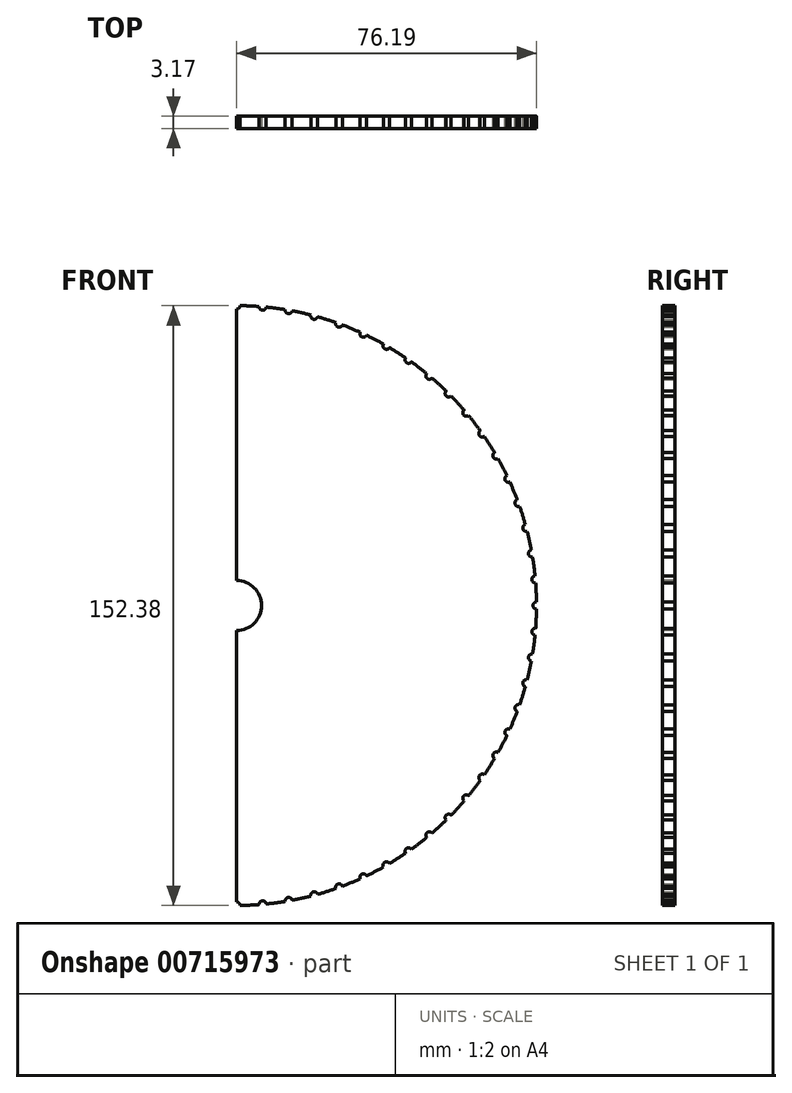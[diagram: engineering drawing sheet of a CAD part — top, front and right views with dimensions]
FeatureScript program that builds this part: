
annotation { "Feature Type Name" : "Feature", "Feature Type Description" : "" }
export const myFeature = defineFeature(function(context is Context, id is Id, definition is map)
    precondition{}
    {
        {
            var Q0;
            Q0=qCreatedBy(makeId("Front.planeOp"),FACE);
            var sketch = newSketch(context, id + "F0", { "sketchPlane" : qUnion([Q0])});
            skArc(sketch, "E0", {"start": v(-42.98, 62.93) * mm, "mid": v(-43.7, 62.42) * mm, "end": v(-44.43, 61.9) * mm});
            skCircle(sketch, "E1", {"center": v(0, 76.2) * mm, "radius": 0.89 * mm});
            skArc(sketch, "E2.1.0", {"start": v(-7.53, 75.83) * mm, "mid": v(-6.56, 75.02) * mm, "end": v(-5.76, 75.98) * mm});
            skCircle(sketch, "E2.2.0", {"center": v(-13.23, 75.04) * mm, "radius": 0.89 * mm});
            skCircle(sketch, "E2.3.0", {"center": v(-19.72, 73.6) * mm, "radius": 0.89 * mm});
            skCircle(sketch, "E2.4.0", {"center": v(-26.06, 71.6) * mm, "radius": 0.89 * mm});
            skCircle(sketch, "E2.5.0", {"center": v(-32.2, 69.06) * mm, "radius": 0.89 * mm});
            skCircle(sketch, "E2.6.0", {"center": v(-38.1, 66) * mm, "radius": 0.89 * mm});
            skCircle(sketch, "E2.7.0", {"center": v(-43.7, 62.42) * mm, "radius": 0.89 * mm});
            skCircle(sketch, "E2.8.0", {"center": v(-48.98, 58.37) * mm, "radius": 0.89 * mm});
            skCircle(sketch, "E2.9.0", {"center": v(-53.88, 53.88) * mm, "radius": 0.89 * mm});
            skCircle(sketch, "E2.10.0", {"center": v(-58.37, 48.98) * mm, "radius": 0.89 * mm});
            skCircle(sketch, "E2.11.0", {"center": v(-62.42, 43.7) * mm, "radius": 0.89 * mm});
            skCircle(sketch, "E2.12.0", {"center": v(-66, 38.1) * mm, "radius": 0.89 * mm});
            skCircle(sketch, "E2.13.0", {"center": v(-69.06, 32.2) * mm, "radius": 0.89 * mm});
            skCircle(sketch, "E2.14.0", {"center": v(-71.6, 26.06) * mm, "radius": 0.89 * mm});
            skCircle(sketch, "E2.15.0", {"center": v(-73.6, 19.72) * mm, "radius": 0.89 * mm});
            skCircle(sketch, "E2.16.0", {"center": v(-75.04, 13.23) * mm, "radius": 0.89 * mm});
            skCircle(sketch, "E2.17.0", {"center": v(-75.91, 6.64) * mm, "radius": 0.89 * mm});
            skCircle(sketch, "E2.18.0", {"center": v(-76.2, 0) * mm, "radius": 0.89 * mm});
            skCircle(sketch, "E2.19.0", {"center": v(-75.91, -6.64) * mm, "radius": 0.89 * mm});
            skCircle(sketch, "E2.20.0", {"center": v(-75.04, -13.23) * mm, "radius": 0.89 * mm});
            skCircle(sketch, "E2.21.0", {"center": v(-73.6, -19.72) * mm, "radius": 0.89 * mm});
            skCircle(sketch, "E2.22.0", {"center": v(-71.6, -26.06) * mm, "radius": 0.89 * mm});
            skCircle(sketch, "E2.23.0", {"center": v(-69.06, -32.2) * mm, "radius": 0.89 * mm});
            skCircle(sketch, "E2.24.0", {"center": v(-66, -38.1) * mm, "radius": 0.89 * mm});
            skCircle(sketch, "E2.25.0", {"center": v(-62.42, -43.7) * mm, "radius": 0.89 * mm});
            skCircle(sketch, "E2.26.0", {"center": v(-58.37, -48.98) * mm, "radius": 0.89 * mm});
            skCircle(sketch, "E2.27.0", {"center": v(-53.88, -53.88) * mm, "radius": 0.89 * mm});
            skCircle(sketch, "E2.28.0", {"center": v(-48.98, -58.37) * mm, "radius": 0.89 * mm});
            skCircle(sketch, "E2.29.0", {"center": v(-43.7, -62.42) * mm, "radius": 0.89 * mm});
            skCircle(sketch, "E2.30.0", {"center": v(-38.1, -66) * mm, "radius": 0.89 * mm});
            skCircle(sketch, "E2.31.0", {"center": v(-32.2, -69.06) * mm, "radius": 0.89 * mm});
            skCircle(sketch, "E2.32.0", {"center": v(-26.06, -71.6) * mm, "radius": 0.89 * mm});
            skCircle(sketch, "E2.33.0", {"center": v(-19.72, -73.6) * mm, "radius": 0.89 * mm});
            skCircle(sketch, "E2.34.0", {"center": v(-13.23, -75.04) * mm, "radius": 0.89 * mm});
            skCircle(sketch, "E2.35.0", {"center": v(-6.64, -75.91) * mm, "radius": 0.89 * mm});
            skCircle(sketch, "E2.36.0", {"center": v(0, -76.2) * mm, "radius": 0.89 * mm});
            skCircle(sketch, "E2.37.0", {"center": v(6.64, -75.91) * mm, "radius": 0.89 * mm});
            skCircle(sketch, "E2.38.0", {"center": v(13.23, -75.04) * mm, "radius": 0.89 * mm});
            skCircle(sketch, "E2.39.0", {"center": v(19.72, -73.6) * mm, "radius": 0.89 * mm});
            skCircle(sketch, "E2.40.0", {"center": v(26.06, -71.6) * mm, "radius": 0.89 * mm});
            skCircle(sketch, "E2.41.0", {"center": v(32.2, -69.06) * mm, "radius": 0.89 * mm});
            skCircle(sketch, "E2.42.0", {"center": v(38.1, -66) * mm, "radius": 0.89 * mm});
            skCircle(sketch, "E2.43.0", {"center": v(43.7, -62.42) * mm, "radius": 0.89 * mm});
            skCircle(sketch, "E2.44.0", {"center": v(48.98, -58.37) * mm, "radius": 0.89 * mm});
            skCircle(sketch, "E2.45.0", {"center": v(53.88, -53.88) * mm, "radius": 0.89 * mm});
            skCircle(sketch, "E2.46.0", {"center": v(58.37, -48.98) * mm, "radius": 0.89 * mm});
            skCircle(sketch, "E2.47.0", {"center": v(62.42, -43.7) * mm, "radius": 0.89 * mm});
            skCircle(sketch, "E2.48.0", {"center": v(66, -38.1) * mm, "radius": 0.89 * mm});
            skCircle(sketch, "E2.49.0", {"center": v(69.06, -32.2) * mm, "radius": 0.89 * mm});
            skCircle(sketch, "E2.50.0", {"center": v(71.6, -26.06) * mm, "radius": 0.89 * mm});
            skCircle(sketch, "E2.51.0", {"center": v(73.6, -19.72) * mm, "radius": 0.89 * mm});
            skCircle(sketch, "E2.52.0", {"center": v(75.04, -13.23) * mm, "radius": 0.89 * mm});
            skCircle(sketch, "E2.53.0", {"center": v(75.91, -6.64) * mm, "radius": 0.89 * mm});
            skCircle(sketch, "E2.54.0", {"center": v(76.2, 0) * mm, "radius": 0.89 * mm});
            skCircle(sketch, "E2.55.0", {"center": v(75.91, 6.64) * mm, "radius": 0.89 * mm});
            skCircle(sketch, "E2.56.0", {"center": v(75.04, 13.23) * mm, "radius": 0.89 * mm});
            skCircle(sketch, "E2.57.0", {"center": v(73.6, 19.72) * mm, "radius": 0.89 * mm});
            skCircle(sketch, "E2.58.0", {"center": v(71.6, 26.06) * mm, "radius": 0.89 * mm});
            skCircle(sketch, "E2.59.0", {"center": v(69.06, 32.2) * mm, "radius": 0.89 * mm});
            skCircle(sketch, "E2.60.0", {"center": v(66, 38.1) * mm, "radius": 0.89 * mm});
            skCircle(sketch, "E2.61.0", {"center": v(62.42, 43.7) * mm, "radius": 0.89 * mm});
            skCircle(sketch, "E2.62.0", {"center": v(58.37, 48.98) * mm, "radius": 0.89 * mm});
            skCircle(sketch, "E2.63.0", {"center": v(53.88, 53.88) * mm, "radius": 0.89 * mm});
            skCircle(sketch, "E2.64.0", {"center": v(48.98, 58.37) * mm, "radius": 0.89 * mm});
            skCircle(sketch, "E2.65.0", {"center": v(43.7, 62.42) * mm, "radius": 0.89 * mm});
            skCircle(sketch, "E2.66.0", {"center": v(38.1, 66) * mm, "radius": 0.89 * mm});
            skCircle(sketch, "E2.67.0", {"center": v(32.2, 69.06) * mm, "radius": 0.89 * mm});
            skCircle(sketch, "E2.68.0", {"center": v(26.06, 71.6) * mm, "radius": 0.89 * mm});
            skCircle(sketch, "E2.69.0", {"center": v(19.72, 73.6) * mm, "radius": 0.89 * mm});
            skCircle(sketch, "E2.70.0", {"center": v(13.23, 75.04) * mm, "radius": 0.89 * mm});
            skCircle(sketch, "E2.71.0", {"center": v(6.64, 75.91) * mm, "radius": 0.89 * mm});
            skArc(sketch, "E3.trimOffspring", {"start": v(-12.36, 75.2) * mm, "mid": v(-13.23, 75.04) * mm, "end": v(-14.1, 74.88) * mm});
            skLineSegment(sketch, "E4", {"start": v(0, 76.2) * mm, "end": v(0, -76.2) * mm});
            skArc(sketch, "E5.trimOffspring", {"start": v(-31.4, 69.43) * mm, "mid": v(-32.2, 69.06) * mm, "end": v(-33, 68.68) * mm});
            skArc(sketch, "E6.trimOffspring", {"start": v(-25.22, 71.9) * mm, "mid": v(-26.06, 71.6) * mm, "end": v(-26.9, 71.3) * mm});
            skArc(sketch, "E7.trimOffspring", {"start": v(-18.86, 73.83) * mm, "mid": v(-19.72, 73.6) * mm, "end": v(-20.58, 73.37) * mm});
            skArc(sketch, "E8.trimOffspring", {"start": v(-0.89, -76.2) * mm, "mid": v(76.15, 2.88) * mm, "end": v(-6.64, 75.91) * mm});
            skArc(sketch, "E9.trimOffspring", {"start": v(-7.53, -75.83) * mm, "mid": v(-6.64, -75.91) * mm, "end": v(-5.76, -75.98) * mm});
            skArc(sketch, "E10.trimOffspring", {"start": v(-14.1, -74.88) * mm, "mid": v(-13.23, -75.04) * mm, "end": v(-12.36, -75.2) * mm});
            skArc(sketch, "E11.trimOffspring", {"start": v(-20.58, -73.37) * mm, "mid": v(-19.72, -73.6) * mm, "end": v(-18.86, -73.83) * mm});
            skArc(sketch, "E12.trimOffspring", {"start": v(-26.9, -71.3) * mm, "mid": v(-26.06, -71.6) * mm, "end": v(-25.22, -71.9) * mm});
            skArc(sketch, "E13.trimOffspring", {"start": v(-33, -68.68) * mm, "mid": v(-32.2, -69.06) * mm, "end": v(-31.4, -69.43) * mm});
            skArc(sketch, "E14.trimOffspring", {"start": v(-38.87, -65.54) * mm, "mid": v(-38.1, -66) * mm, "end": v(-37.33, -66.43) * mm});
            skArc(sketch, "E15.trimOffspring", {"start": v(-44.43, -61.9) * mm, "mid": v(-43.7, -62.42) * mm, "end": v(-42.98, -62.93) * mm});
            skArc(sketch, "E16.trimOffspring", {"start": v(-49.66, -57.8) * mm, "mid": v(-48.98, -58.37) * mm, "end": v(-48.3, -58.94) * mm});
            skArc(sketch, "E17.trimOffspring", {"start": v(-54.5, -53.25) * mm, "mid": v(-53.88, -53.88) * mm, "end": v(-53.25, -54.5) * mm});
            skArc(sketch, "E18.trimOffspring", {"start": v(-58.94, -48.3) * mm, "mid": v(-58.37, -48.98) * mm, "end": v(-57.8, -49.66) * mm});
            skArc(sketch, "E19.trimOffspring", {"start": v(-66.43, -37.33) * mm, "mid": v(-66, -38.1) * mm, "end": v(-65.54, -38.87) * mm});
            skArc(sketch, "E20.trimOffspring", {"start": v(-62.93, -42.98) * mm, "mid": v(-62.42, -43.7) * mm, "end": v(-61.9, -44.43) * mm});
            skArc(sketch, "E21.trimOffspring", {"start": v(-69.43, -31.4) * mm, "mid": v(-69.06, -32.2) * mm, "end": v(-68.68, -33) * mm});
            skArc(sketch, "E22.trimOffspring", {"start": v(-71.9, -25.22) * mm, "mid": v(-71.6, -26.06) * mm, "end": v(-71.3, -26.9) * mm});
            skArc(sketch, "E23.trimOffspring", {"start": v(-73.83, -18.86) * mm, "mid": v(-73.6, -19.72) * mm, "end": v(-73.37, -20.58) * mm});
            skArc(sketch, "E24.trimOffspring", {"start": v(-75.2, -12.36) * mm, "mid": v(-75.04, -13.23) * mm, "end": v(-74.88, -14.1) * mm});
            skArc(sketch, "E25.trimOffspring", {"start": v(-75.98, -5.76) * mm, "mid": v(-75.91, -6.64) * mm, "end": v(-75.83, -7.53) * mm});
            skArc(sketch, "E26.trimOffspring", {"start": v(-76.2, 0.89) * mm, "mid": v(-76.2, 0) * mm, "end": v(-76.2, -0.89) * mm});
            skArc(sketch, "E27.trimOffspring", {"start": v(-75.83, 7.53) * mm, "mid": v(-75.91, 6.64) * mm, "end": v(-75.98, 5.76) * mm});
            skArc(sketch, "E28.trimOffspring", {"start": v(-71.3, 26.9) * mm, "mid": v(-71.45, 26.48) * mm, "end": v(-71.6, 26.06) * mm});
            skArc(sketch, "E29.trimOffspring", {"start": v(-65.54, 38.87) * mm, "mid": v(-66, 38.1) * mm, "end": v(-66.43, 37.33) * mm});
            skArc(sketch, "E30.trimOffspring", {"start": v(-61.9, 44.43) * mm, "mid": v(-62.42, 43.7) * mm, "end": v(-62.93, 42.98) * mm});
            skArc(sketch, "E31.trimOffspring", {"start": v(-57.8, 49.66) * mm, "mid": v(-58.37, 48.98) * mm, "end": v(-58.94, 48.3) * mm});
            skArc(sketch, "E32.trimOffspring", {"start": v(-53.25, 54.5) * mm, "mid": v(-53.88, 53.88) * mm, "end": v(-54.5, 53.25) * mm});
            skArc(sketch, "E33.trimOffspring", {"start": v(-37.33, 66.43) * mm, "mid": v(-38.1, 66) * mm, "end": v(-38.87, 65.54) * mm});
            skArc(sketch, "E34.trimOffspring", {"start": v(-48.3, 58.94) * mm, "mid": v(-48.98, 58.37) * mm, "end": v(-49.66, 57.8) * mm});
            skArc(sketch, "E35.trimOffspring", {"start": v(-68.68, 33) * mm, "mid": v(-69.06, 32.2) * mm, "end": v(-69.43, 31.4) * mm});
            skArc(sketch, "E36.trimOffspring", {"start": v(-73.37, 20.58) * mm, "mid": v(-73.6, 19.72) * mm, "end": v(-73.83, 18.86) * mm});
            skArc(sketch, "E37.trimOffspring", {"start": v(-74.88, 14.1) * mm, "mid": v(-75.04, 13.23) * mm, "end": v(-75.2, 12.36) * mm});
            skSolve(sketch);
        }
        {
            var Q0;
            Q0=qCreatedBy(makeId("Front.planeOp"),FACE);
            var sketch = newSketch(context, id + "F1", { "sketchPlane" : qUnion([Q0])});
            skLineSegment(sketch, "E38", {"start": v(0, 0) * mm, "end": v(6.64, 75.91) * mm});
            skLineSegment(sketch, "E39", {"start": v(0, 0) * mm, "end": v(13.23, 75.04) * mm});
            skLineSegment(sketch, "E40", {"start": v(0, 0) * mm, "end": v(19.72, 73.6) * mm});
            skLineSegment(sketch, "E41", {"start": v(0, 0) * mm, "end": v(26.06, 71.6) * mm});
            skLineSegment(sketch, "E42", {"start": v(0, 0) * mm, "end": v(32.2, 69.06) * mm});
            skLineSegment(sketch, "E43", {"start": v(0, 0) * mm, "end": v(38.1, 66) * mm});
            skLineSegment(sketch, "E44", {"start": v(0, 0) * mm, "end": v(43.7, 62.42) * mm});
            skLineSegment(sketch, "E45", {"start": v(0, 0) * mm, "end": v(48.98, 58.37) * mm});
            skLineSegment(sketch, "E46", {"start": v(0, 0) * mm, "end": v(53.88, 53.88) * mm});
            skLineSegment(sketch, "E47", {"start": v(0, 0) * mm, "end": v(58.37, 48.98) * mm});
            skLineSegment(sketch, "E48", {"start": v(0, 0) * mm, "end": v(62.42, 43.7) * mm});
            skLineSegment(sketch, "E49", {"start": v(0, 0) * mm, "end": v(66, 38.1) * mm});
            skLineSegment(sketch, "E50", {"start": v(0, 0) * mm, "end": v(69.06, 32.2) * mm});
            skLineSegment(sketch, "E51", {"start": v(0, 0) * mm, "end": v(71.6, 26.06) * mm});
            skLineSegment(sketch, "E52", {"start": v(0, 0) * mm, "end": v(73.6, 19.72) * mm});
            skLineSegment(sketch, "E53", {"start": v(0, 0) * mm, "end": v(75.91, -6.64) * mm});
            skLineSegment(sketch, "E54", {"start": v(0, 0) * mm, "end": v(75.04, -13.23) * mm});
            skLineSegment(sketch, "E55", {"start": v(0, 0) * mm, "end": v(73.6, -19.72) * mm});
            skLineSegment(sketch, "E56", {"start": v(0, 0) * mm, "end": v(71.6, -26.06) * mm});
            skLineSegment(sketch, "E57", {"start": v(0, 0) * mm, "end": v(69.06, -32.2) * mm});
            skLineSegment(sketch, "E58", {"start": v(0, 0) * mm, "end": v(66, -38.1) * mm});
            skLineSegment(sketch, "E59", {"start": v(0, 0) * mm, "end": v(62.42, -43.7) * mm});
            skLineSegment(sketch, "E60", {"start": v(0, 0) * mm, "end": v(58.37, -48.98) * mm});
            skLineSegment(sketch, "E61", {"start": v(0, 0) * mm, "end": v(53.88, -53.88) * mm});
            skLineSegment(sketch, "E62", {"start": v(0, 0) * mm, "end": v(48.98, -58.37) * mm});
            skLineSegment(sketch, "E63", {"start": v(0, 0) * mm, "end": v(43.7, -62.42) * mm});
            skLineSegment(sketch, "E64", {"start": v(0, 0) * mm, "end": v(38.1, -66) * mm});
            skLineSegment(sketch, "E65", {"start": v(0, 0) * mm, "end": v(32.24, -69.14) * mm});
            skLineSegment(sketch, "E66", {"start": v(0, 0) * mm, "end": v(26.08, -71.64) * mm});
            skLineSegment(sketch, "E67", {"start": v(0, 0) * mm, "end": v(19.72, -73.6) * mm});
            skLineSegment(sketch, "E68", {"start": v(0, 0) * mm, "end": v(12.98, -73.6) * mm});
            skLineSegment(sketch, "E69", {"start": v(12.98, -73.6) * mm, "end": v(13, -74.6) * mm});
            skLineSegment(sketch, "E70", {"start": v(0, 0) * mm, "end": v(6.63, -75.82) * mm});
            skLineSegment(sketch, "E71", {"start": v(0, 0) * mm, "end": v(0, -75.82) * mm});
            skLineSegment(sketch, "E72", {"start": v(0, 0) * mm, "end": v(2.2, -0.2) * mm});
            skLineSegment(sketch, "E73", {"start": v(0, 0) * mm, "end": v(75.04, 13.23) * mm});
            skLineSegment(sketch, "E74", {"start": v(0, 0) * mm, "end": v(75.9, 6.64) * mm});
            skSolve(sketch);
        }
        {
            var Q0;
            Q0 = qSketchRegion(id + "F1", true);
            var Q1;
            {var subQ0=sQuery(id+"F0.wireOp",EDGE,"E4");var subQ1=sQuery(id+"F0.wireOp",EDGE,"E1");var subQ2=makeQuery(id+"F0.imprint","INTERSECT",VERTEX,{"derivedFrom":[subQ1,subQ0]});Q1=makeQuery(id+"F0.imprint","IMPRINT",FACE,{"disambiguationData":[TD([[makeQuery(id+"F0.imprint","IMPRINT",EDGE,{"disambiguationData":[TD([[subQ2,-1.0]])],"derivedFrom":subQ1}),-1.0]])]});}
            extrude(context, id + "F2", {"entities" : qUnion([Q0, Q1]), "depth" : 3.17 * mm, "offsetDistance" : 25.4 * mm});
        }
        {
            var Q0;
            Q0=sQuery(id+"F1.wireOp",VERTEX,"E63.start");
            var Q1;
            Q1=makeQuery(id+"F2.opExtrude","SWEPT_BODY",BODY,{"disambiguationData":[OSD([sQuery(id+"F0.wireOp",EDGE,"E1"),sQuery(id+"F0.wireOp",EDGE,"E2.36.0"),sQuery(id+"F0.wireOp",EDGE,"E2.37.0"),sQuery(id+"F0.wireOp",EDGE,"E2.38.0"),sQuery(id+"F0.wireOp",EDGE,"E2.39.0"),sQuery(id+"F0.wireOp",EDGE,"E2.40.0"),sQuery(id+"F0.wireOp",EDGE,"E2.41.0"),sQuery(id+"F0.wireOp",EDGE,"E2.42.0"),sQuery(id+"F0.wireOp",EDGE,"E2.43.0"),sQuery(id+"F0.wireOp",EDGE,"E2.44.0"),sQuery(id+"F0.wireOp",EDGE,"E2.45.0"),sQuery(id+"F0.wireOp",EDGE,"E2.46.0"),sQuery(id+"F0.wireOp",EDGE,"E2.47.0"),sQuery(id+"F0.wireOp",EDGE,"E2.48.0"),sQuery(id+"F0.wireOp",EDGE,"E2.49.0"),sQuery(id+"F0.wireOp",EDGE,"E2.50.0"),sQuery(id+"F0.wireOp",EDGE,"E2.51.0"),sQuery(id+"F0.wireOp",EDGE,"E2.52.0"),sQuery(id+"F0.wireOp",EDGE,"E2.53.0"),sQuery(id+"F0.wireOp",EDGE,"E2.54.0"),sQuery(id+"F0.wireOp",EDGE,"E2.55.0"),sQuery(id+"F0.wireOp",EDGE,"E2.56.0"),sQuery(id+"F0.wireOp",EDGE,"E2.57.0"),sQuery(id+"F0.wireOp",EDGE,"E2.58.0"),sQuery(id+"F0.wireOp",EDGE,"E2.59.0"),sQuery(id+"F0.wireOp",EDGE,"E2.60.0"),sQuery(id+"F0.wireOp",EDGE,"E2.61.0"),sQuery(id+"F0.wireOp",EDGE,"E2.62.0"),sQuery(id+"F0.wireOp",EDGE,"E2.63.0"),sQuery(id+"F0.wireOp",EDGE,"E2.64.0"),sQuery(id+"F0.wireOp",EDGE,"E2.65.0"),sQuery(id+"F0.wireOp",EDGE,"E2.66.0"),sQuery(id+"F0.wireOp",EDGE,"E2.67.0"),sQuery(id+"F0.wireOp",EDGE,"E2.68.0"),sQuery(id+"F0.wireOp",EDGE,"E2.69.0"),sQuery(id+"F0.wireOp",EDGE,"E2.70.0"),sQuery(id+"F0.wireOp",EDGE,"E2.71.0"),sQuery(id+"F0.wireOp",EDGE,"E4"),sQuery(id+"F0.wireOp",EDGE,"E8.trimOffspring")])]});
            hole(context, id + "F3", {"style" : HoleStyle.SIMPLE, "endStyle" : HoleEndStyle.THROUGH, "oppositeDirection" : true, "holeDiameter" : 12.7 * mm, "majorDiameter" : 6.35 * mm, "isTappedThrough" : true, "tappedDepth" : 12.7 * mm, "tapClearance" : 3, "locations" : qUnion([Q0]), "scope" : qUnion([Q1]), "startStyle" : HoleStartStyle.SKETCH});
        }
    });
